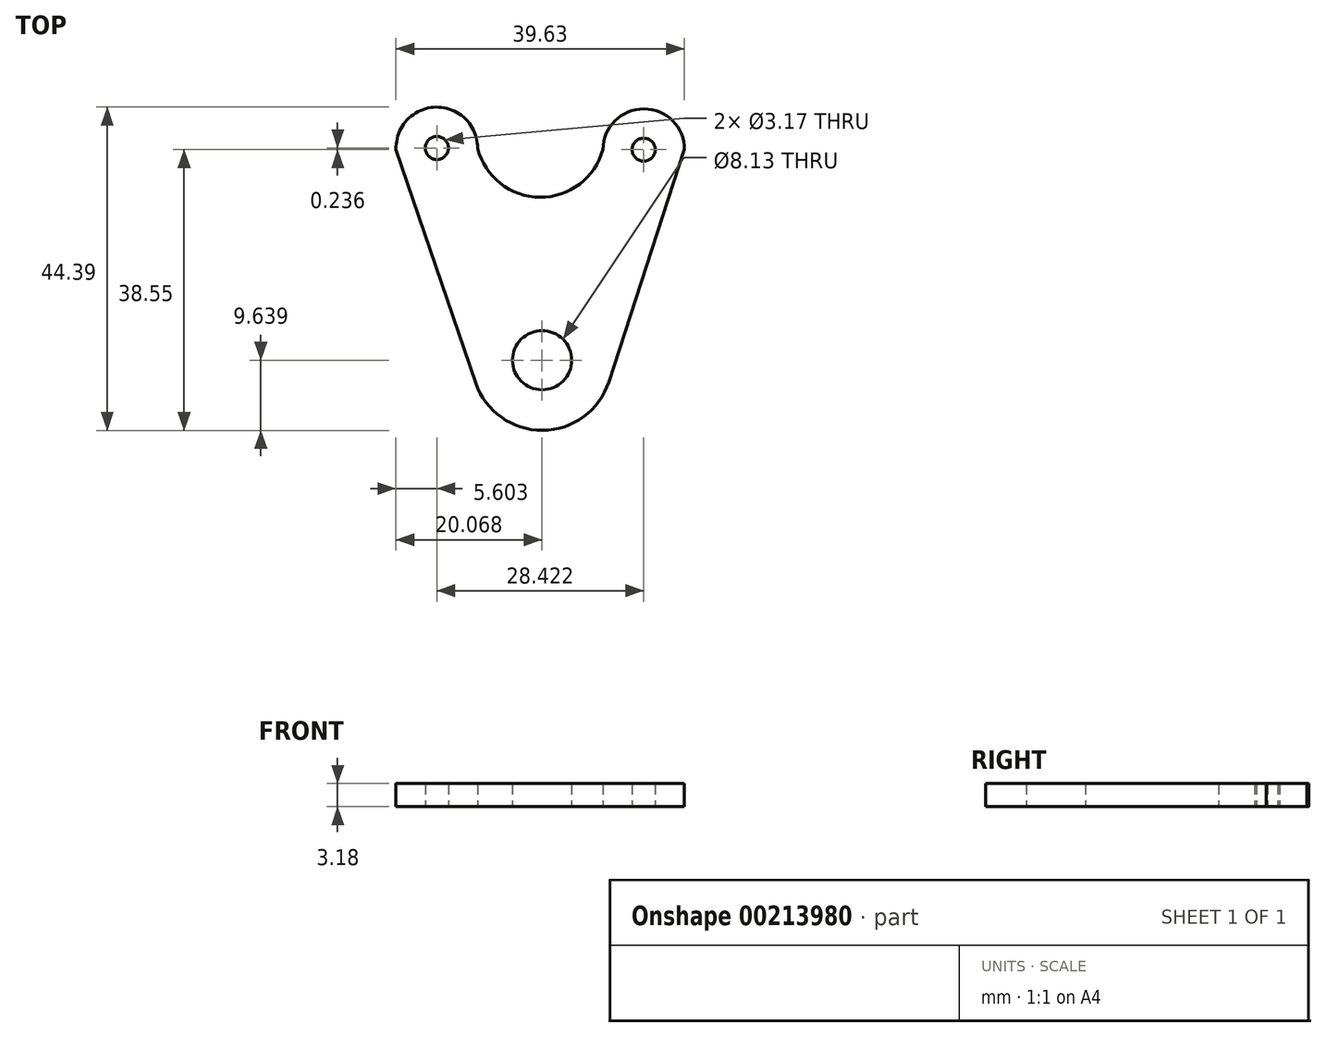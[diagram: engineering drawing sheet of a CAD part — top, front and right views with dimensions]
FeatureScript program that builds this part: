
annotation { "Feature Type Name" : "Feature", "Feature Type Description" : "" }
export const myFeature = defineFeature(function(context is Context, id is Id, definition is map)
    precondition{}
    {
        {
            var Q0;
            Q0=qCreatedBy(makeId("Top.planeOp"),FACE);
            var sketch = newSketch(context, id + "F0", { "sketchPlane" : qUnion([Q0])});
            skArc(sketch, "E0", {"start": v(-27.62, 38.29) * mm, "mid": v(-33.32, 43.94) * mm, "end": v(-38.83, 38.1) * mm});
            skArc(sketch, "E1", {"start": v(0.8, 38.1) * mm, "mid": v(-4.78, 43.7) * mm, "end": v(-10.4, 38.15) * mm});
            skArc(sketch, "E2", {"start": v(-27.9, 6.12) * mm, "mid": v(-18.72, -0.45) * mm, "end": v(-9.6, 6.2) * mm});
            skLineSegment(sketch, "E3", {"start": v(-38.83, 38.1) * mm, "end": v(-27.88, 6.07) * mm});
            skLineSegment(sketch, "E4", {"start": v(0.8, 38.1) * mm, "end": v(-9.6, 6.2) * mm});
            skArc(sketch, "E5", {"start": v(-27.62, 38.29) * mm, "mid": v(-19.07, 31.56) * mm, "end": v(-10.4, 38.15) * mm});
            skCircle(sketch, "E6", {"center": v(-33.23, 38.34) * mm, "radius": 1.59 * mm});
            skCircle(sketch, "E7", {"center": v(-4.8, 38.1) * mm, "radius": 1.59 * mm});
            skCircle(sketch, "E8", {"center": v(-18.76, 9.19) * mm, "radius": 4.06 * mm});
            skSolve(sketch);
        }
        {
            var Q0;
            Q0=makeQuery(id+"F0.imprint","IMPRINT",FACE,{"disambiguationData":[TD([[makeQuery(id+"F0.imprint","IMPRINT",EDGE,{"derivedFrom":sQuery(id+"F0.wireOp",EDGE,"E0")}),1.0]])]});
            extrude(context, id + "F1", {"entities" : qUnion([Q0]), "depth" : 3.17 * mm});
        }
    });
